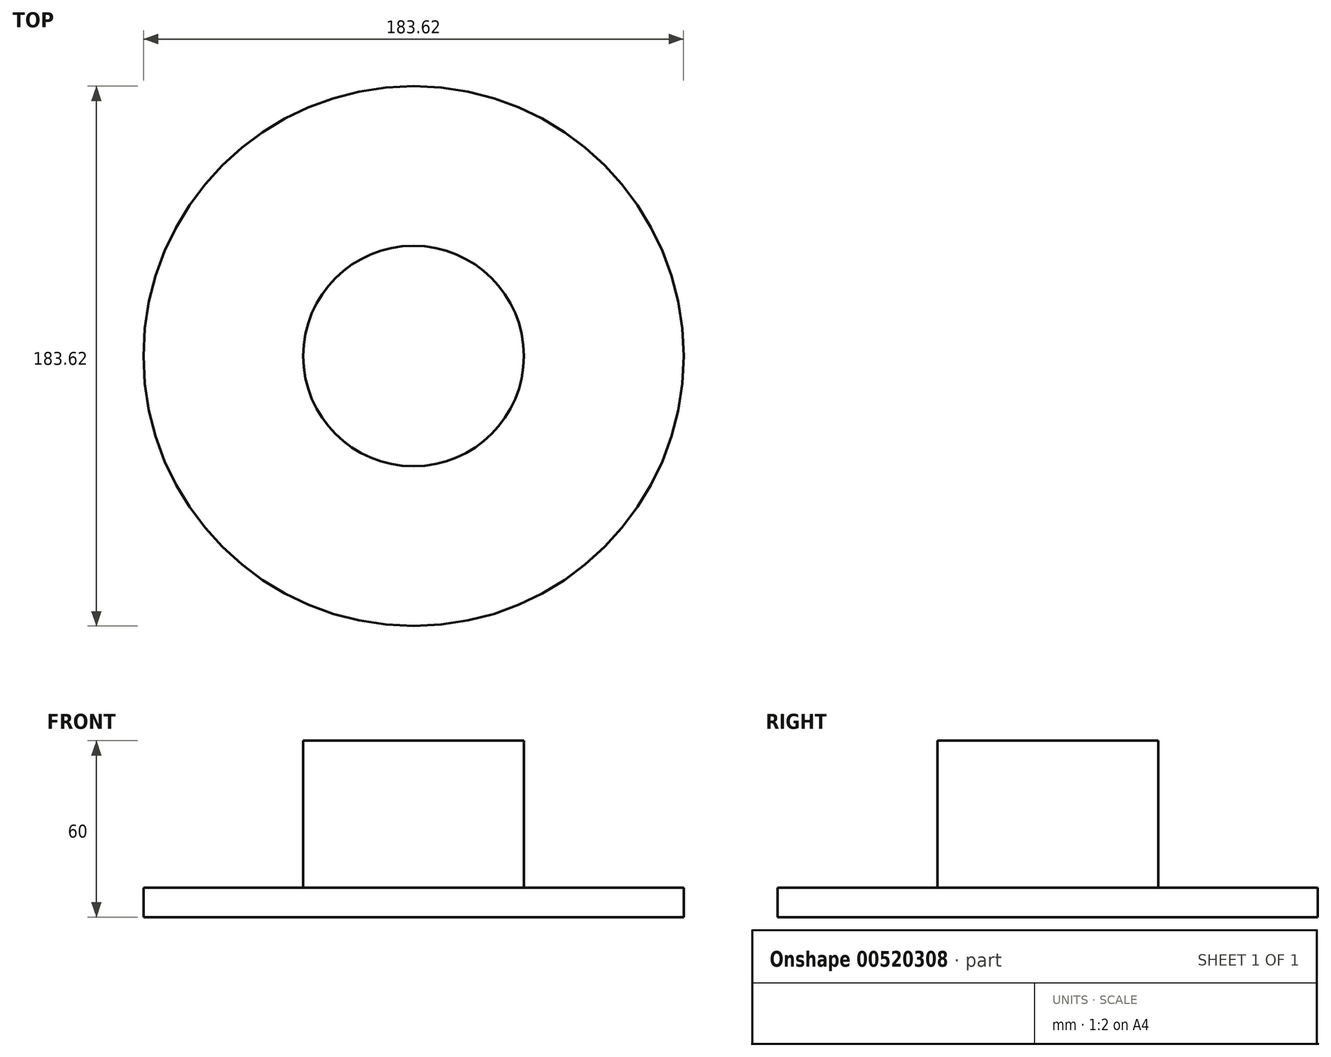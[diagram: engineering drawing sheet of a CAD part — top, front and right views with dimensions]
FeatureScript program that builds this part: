
annotation { "Feature Type Name" : "Feature", "Feature Type Description" : "" }
export const myFeature = defineFeature(function(context is Context, id is Id, definition is map)
    precondition{}
    {
        {
            var Q0;
            Q0=qCreatedBy(makeId("Top.planeOp"),FACE);
            var sketch = newSketch(context, id + "F0", { "sketchPlane" : qUnion([Q0])});
            skCircle(sketch, "E0", {"center": v(0, 0) * mm, "radius": 91.81 * mm});
            skSolve(sketch);
        }
        {
            var Q0;
            Q0=makeQuery(id+"F0.imprint","IMPRINT",FACE,{"disambiguationData":[TD([[makeQuery(id+"F0.imprint","IMPRINT",EDGE,{"derivedFrom":sQuery(id+"F0.wireOp",EDGE,"E0")}),1.0]])]});
            extrude(context, id + "F1", {"entities" : qUnion([Q0]), "oppositeDirection" : true, "depth" : 10 * mm, "offsetDistance" : 25 * mm});
        }
        {
            var Q0;
            Q0=qCreatedBy(makeId("Top.planeOp"),FACE);
            var sketch = newSketch(context, id + "F2", { "sketchPlane" : qUnion([Q0])});
            skCircle(sketch, "E1", {"center": v(0, 0) * mm, "radius": 37.5 * mm});
            skSolve(sketch);
        }
        {
            var Q0;
            Q0=makeQuery(id+"F2.imprint","IMPRINT",FACE,{"disambiguationData":[TD([[makeQuery(id+"F2.imprint","IMPRINT",EDGE,{"derivedFrom":sQuery(id+"F2.wireOp",EDGE,"E1")}),1.0]])]});
            extrude(context, id + "F3", {"entities" : qUnion([Q0]), "operationType" : NewBodyOperationType.ADD, "depth" : 50 * mm, "offsetDistance" : 25 * mm});
        }
    });
